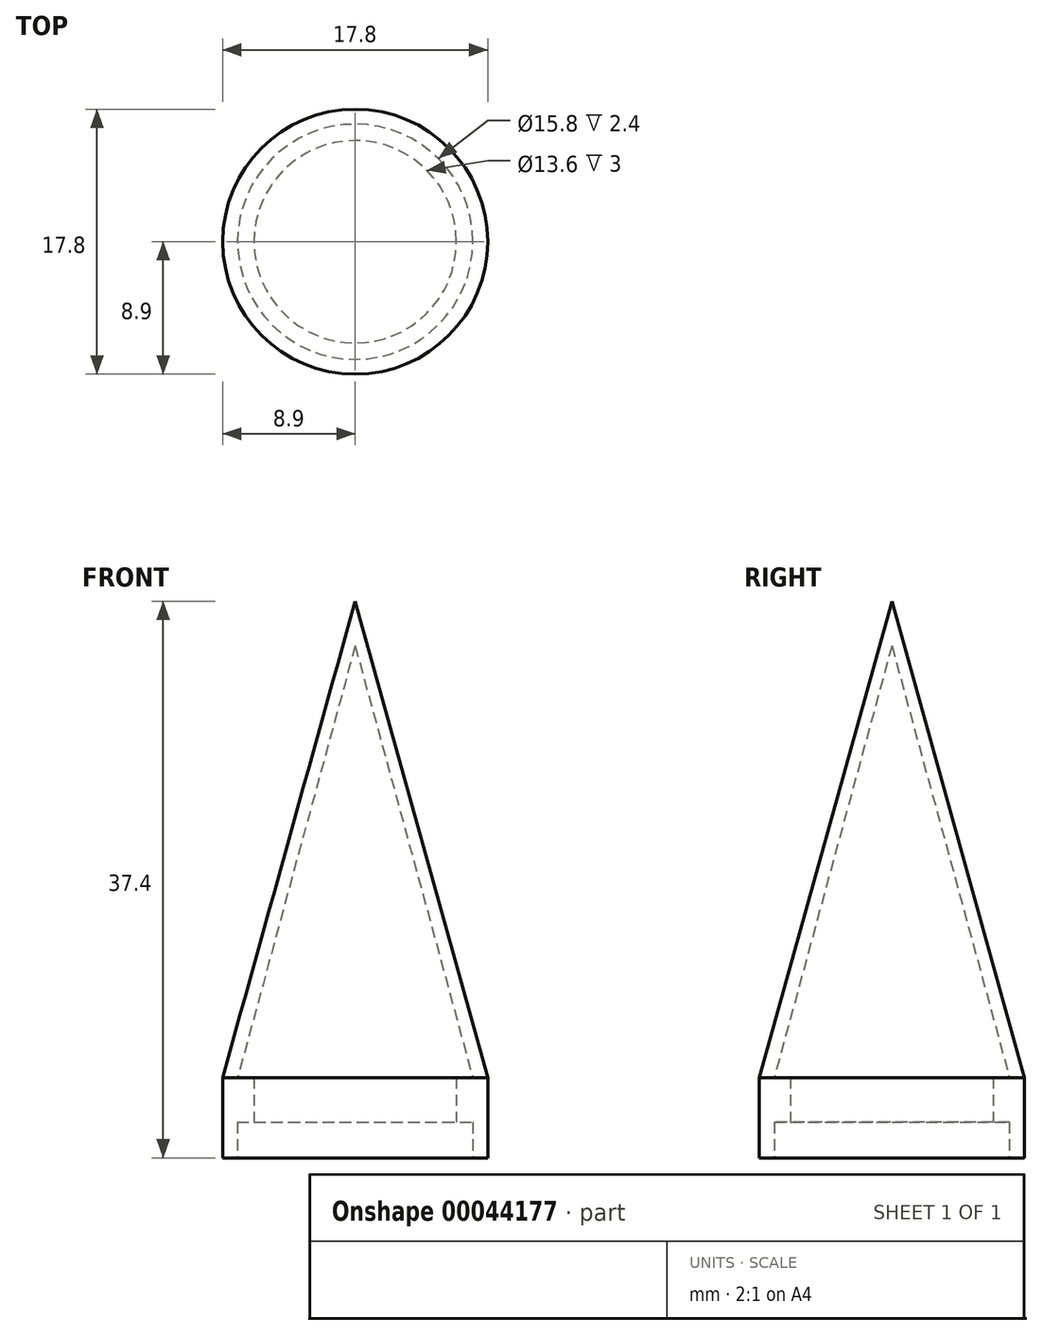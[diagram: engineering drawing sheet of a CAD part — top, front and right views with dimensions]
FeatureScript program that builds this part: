
annotation { "Feature Type Name" : "Feature", "Feature Type Description" : "" }
export const myFeature = defineFeature(function(context is Context, id is Id, definition is map)
    precondition{}
    {
        {
            var Q0;
            Q0=qCreatedBy(makeId("Top.planeOp"),FACE);
            var sketch = newSketch(context, id + "F0", { "sketchPlane" : qUnion([Q0])});
            skLineSegment(sketch, "E0", {"start": v(-17.52, 0) * mm, "end": v(42.68, 0) * mm, "construction": true});
            skLineSegment(sketch, "E1", {"start": v(0, 0) * mm, "end": v(0, 7.9) * mm, "construction": true});
            skLineSegment(sketch, "E2", {"start": v(0, 7.9) * mm, "end": v(2.4, 7.9) * mm});
            skLineSegment(sketch, "E3", {"start": v(2.4, 6.8) * mm, "end": v(2.4, 7.9) * mm});
            skLineSegment(sketch, "E4", {"start": v(2.4, 6.8) * mm, "end": v(5.4, 6.8) * mm});
            skLineSegment(sketch, "E5", {"start": v(0, 7.9) * mm, "end": v(0, 8.9) * mm});
            skLineSegment(sketch, "E6", {"start": v(5.4, 6.8) * mm, "end": v(5.4, 7.9) * mm});
            skLineSegment(sketch, "E7", {"start": v(0, 8.9) * mm, "end": v(5.4, 8.9) * mm});
            skLineSegment(sketch, "E8", {"start": v(5.4, 8.9) * mm, "end": v(37.4, 0) * mm});
            skLineSegment(sketch, "E9", {"start": v(37.4, 0) * mm, "end": v(34.4, 0) * mm});
            skLineSegment(sketch, "E10", {"start": v(34.4, 0) * mm, "end": v(5.4, 7.9) * mm});
            skSolve(sketch);
        }
        {
            var Q0;
            Q0=makeQuery(id+"F0.imprint","IMPRINT",FACE,{"disambiguationData":[TD([[makeQuery(id+"F0.imprint","IMPRINT",EDGE,{"derivedFrom":sQuery(id+"F0.wireOp",EDGE,"E2")}),1.0]])]});
            var Q1;
            Q1=sQuery(id+"F0.wireOp",EDGE,"E0");
            revolve(context, id + "F1", {"entities" : qUnion([Q0]), "axis" : qUnion([Q1]), "revolveType" : RevolveType.FULL});
        }
        {
            var Q0;
            Q0=qCreatedBy(makeId("Front.planeOp"),FACE);
            var sketch = newSketch(context, id + "F2", { "sketchPlane" : qUnion([Q0])});
            skCircle(sketch, "E11", {"center": v(0, 0) * mm, "radius": 6.95 * mm});
            skSolve(sketch);
        }
        {
            var Q0;
            Q0=makeQuery(id+"F1.opRevolve","SWEPT_BODY",BODY,{"disambiguationData":[OSD([sQuery(id+"F0.wireOp",EDGE,"E2"),sQuery(id+"F0.wireOp",EDGE,"E3"),sQuery(id+"F0.wireOp",EDGE,"E4"),sQuery(id+"F0.wireOp",EDGE,"E5"),sQuery(id+"F0.wireOp",EDGE,"E6"),sQuery(id+"F0.wireOp",EDGE,"E7"),sQuery(id+"F0.wireOp",EDGE,"E8"),sQuery(id+"F0.wireOp",EDGE,"E9"),sQuery(id+"F0.wireOp",EDGE,"E10")])]});
            var Q1;
            Q1=sQuery(id+"F2.wireOp",EDGE,"E11");
            transform(context, id + "F3", {"entities" : qUnion([Q0]), "transformType" : TransformType.ROTATION, "transformAxis" : qUnion([Q1]), "angle" : 90 * degree, "makeCopy" : false});
        }
    });
